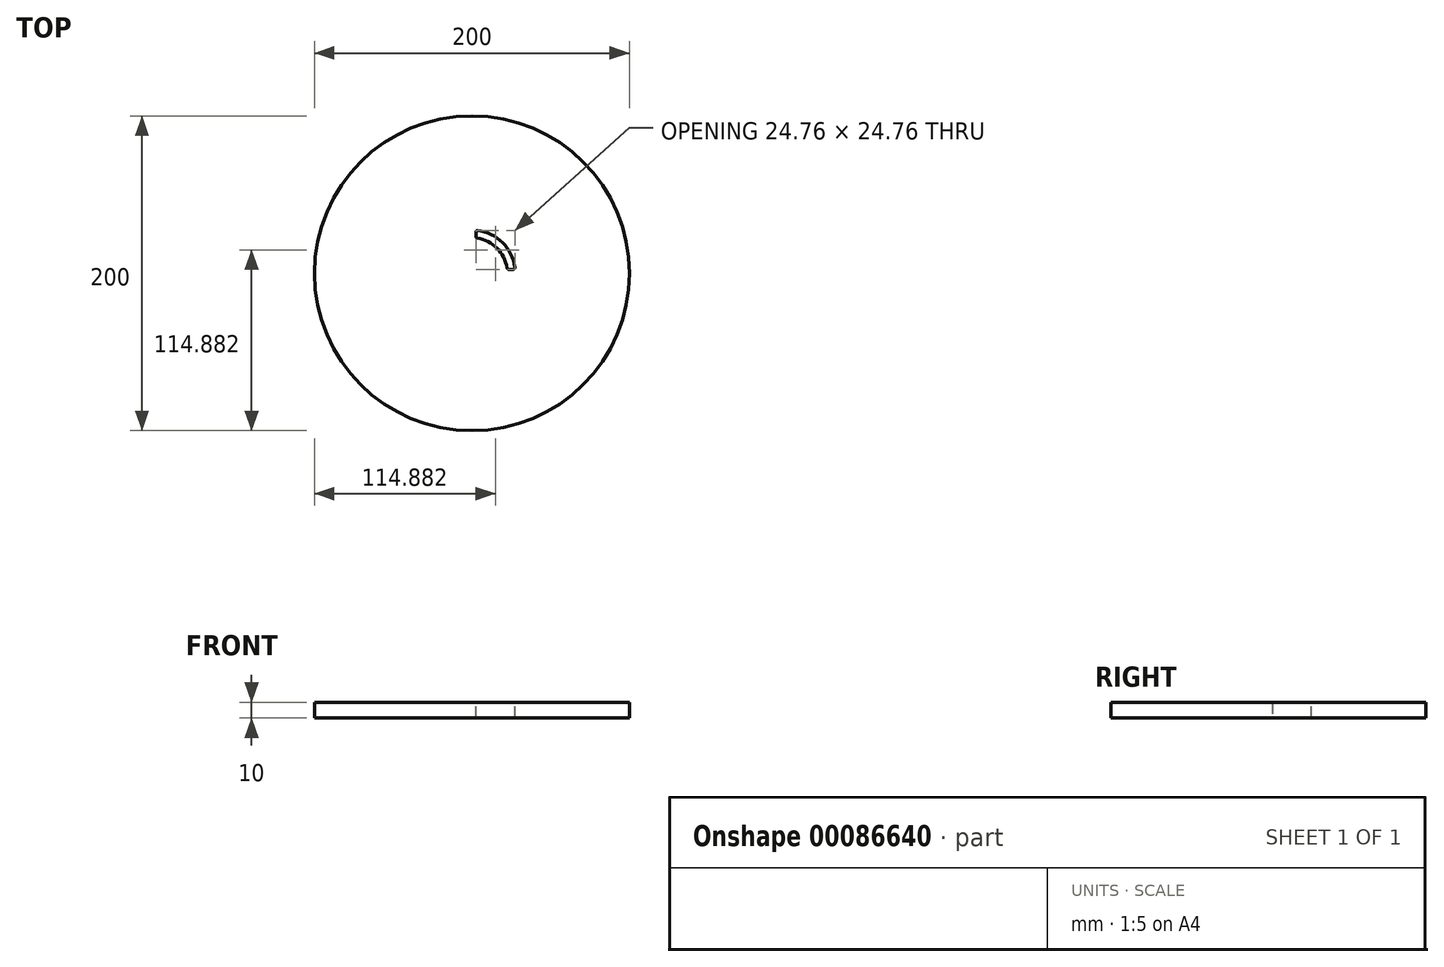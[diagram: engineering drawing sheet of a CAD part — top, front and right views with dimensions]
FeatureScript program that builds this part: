
annotation { "Feature Type Name" : "Feature", "Feature Type Description" : "" }
export const myFeature = defineFeature(function(context is Context, id is Id, definition is map)
    precondition{}
    {
        {
            var Q0;
            Q0=qCreatedBy(makeId("Top.planeOp"),FACE);
            var sketch = newSketch(context, id + "F0", { "sketchPlane" : qUnion([Q0])});
            skCircle(sketch, "E0", {"center": v(0, 0) * mm, "radius": 100 * mm});
            skSolve(sketch);
        }
        {
            var Q0;
            Q0 = qSketchRegion(id + "F0", true);
            extrude(context, id + "F1", {"entities" : qUnion([Q0]), "depth" : 10 * mm});
        }
        {
            assignVariable(context, id + "F2", {"name" : "Diam", "anyValue" : 15});
        }
        {
            assignVariable(context, id + "F3", {"name" : "Diam", "anyValue" : getVariable(context, 'Diam') + 30});
        }
        {
            assignVariable(context, id + "F4", {"name" : "Slots", "anyValue" : 0});
        }
        {
            assignVariable(context, id + "F5", {"name" : "Slots", "anyValue" : getVariable(context, 'Slots') + 4});
        }
        {
            var Q0;
            Q0=makeQuery(id+"F1.opExtrude","CAP_FACE",FACE,{"disambiguationData":[OSD([sQuery(id+"F0.wireOp",EDGE,"E0")])],"isStart":false});
            var sketch = newSketch(context, id + "F6", { "sketchPlane" : qUnion([Q0])});
            skLineSegment(sketch, "E1", {"start": v(0, 27.3) * mm, "end": v(0, 0) * mm, "construction": true});
            skArc(sketch, "E2", {"start": v(2.5, 27.39) * mm, "mid": v(19.45, 19.45) * mm, "end": v(27.39, 2.5) * mm});
            skArc(sketch, "E3", {"start": v(2.5, 22.36) * mm, "mid": v(15.9, 15.9) * mm, "end": v(22.36, 2.5) * mm});
            skLineSegment(sketch, "E4", {"start": v(2.5, 27.39) * mm, "end": v(2.5, 22.36) * mm});
            skLineSegment(sketch, "E5", {"start": v(22.36, 2.5) * mm, "end": v(27.39, 2.5) * mm});
            skLineSegment(sketch, "E6", {"start": v(0, 0) * mm, "end": v(30.23, 0) * mm, "construction": true});
            skSolve(sketch);
        }
        {
            var Q0;
            Q0 = qSketchRegion(id + "F6", true);
            extrude(context, id + "F7", {"entities" : qUnion([Q0]), "operationType" : NewBodyOperationType.REMOVE, "endBound" : BoundingType.THROUGH_ALL, "oppositeDirection" : true, "depth" : 25 * mm});
        }
        {
            var Q0;
            Q0=makeQuery(id+"F7.boolean.opBoolean","COPY",EDGE,{"derivedFrom":makeQuery(id+"F7.opExtrude","SWEPT_EDGE",EDGE,{"disambiguationData":[OSD([sQuery(id+"F6.wireOp",EDGE,"E2"),sQuery(id+"F6.wireOp",EDGE,"E4")])]})});
            var Q1;
            Q1=makeQuery(id+"F7.boolean.opBoolean","COPY",EDGE,{"derivedFrom":makeQuery(id+"F7.opExtrude","SWEPT_EDGE",EDGE,{"disambiguationData":[OSD([sQuery(id+"F6.wireOp",EDGE,"E3"),sQuery(id+"F6.wireOp",EDGE,"E4")])]})});
            var Q2;
            Q2=makeQuery(id+"F7.boolean.opBoolean","COPY",EDGE,{"derivedFrom":makeQuery(id+"F7.opExtrude","SWEPT_EDGE",EDGE,{"disambiguationData":[OSD([sQuery(id+"F6.wireOp",EDGE,"E3"),sQuery(id+"F6.wireOp",EDGE,"E5")])]})});
            var Q3;
            Q3=makeQuery(id+"F7.boolean.opBoolean","COPY",EDGE,{"derivedFrom":makeQuery(id+"F7.opExtrude","SWEPT_EDGE",EDGE,{"disambiguationData":[OSD([sQuery(id+"F6.wireOp",EDGE,"E2"),sQuery(id+"F6.wireOp",EDGE,"E5")])]})});
            var Q4;
            Q4=makeQuery(id+"F7.boolean.opBoolean","COPY",EDGE,{"derivedFrom":makeQuery(id+"F7.opExtrude","CAP_EDGE",EDGE,{"disambiguationData":[OSD([sQuery(id+"F6.wireOp",EDGE,"E3")])],"isStart":true})});
            fillet(context, id + "F8", {"entities" : qUnion([Q0, Q1, Q2, Q3, Q4]), "radius" : 1 * mm, "tangentPropagation" : true, "allowEdgeOverflow" : false});
        }
    });
